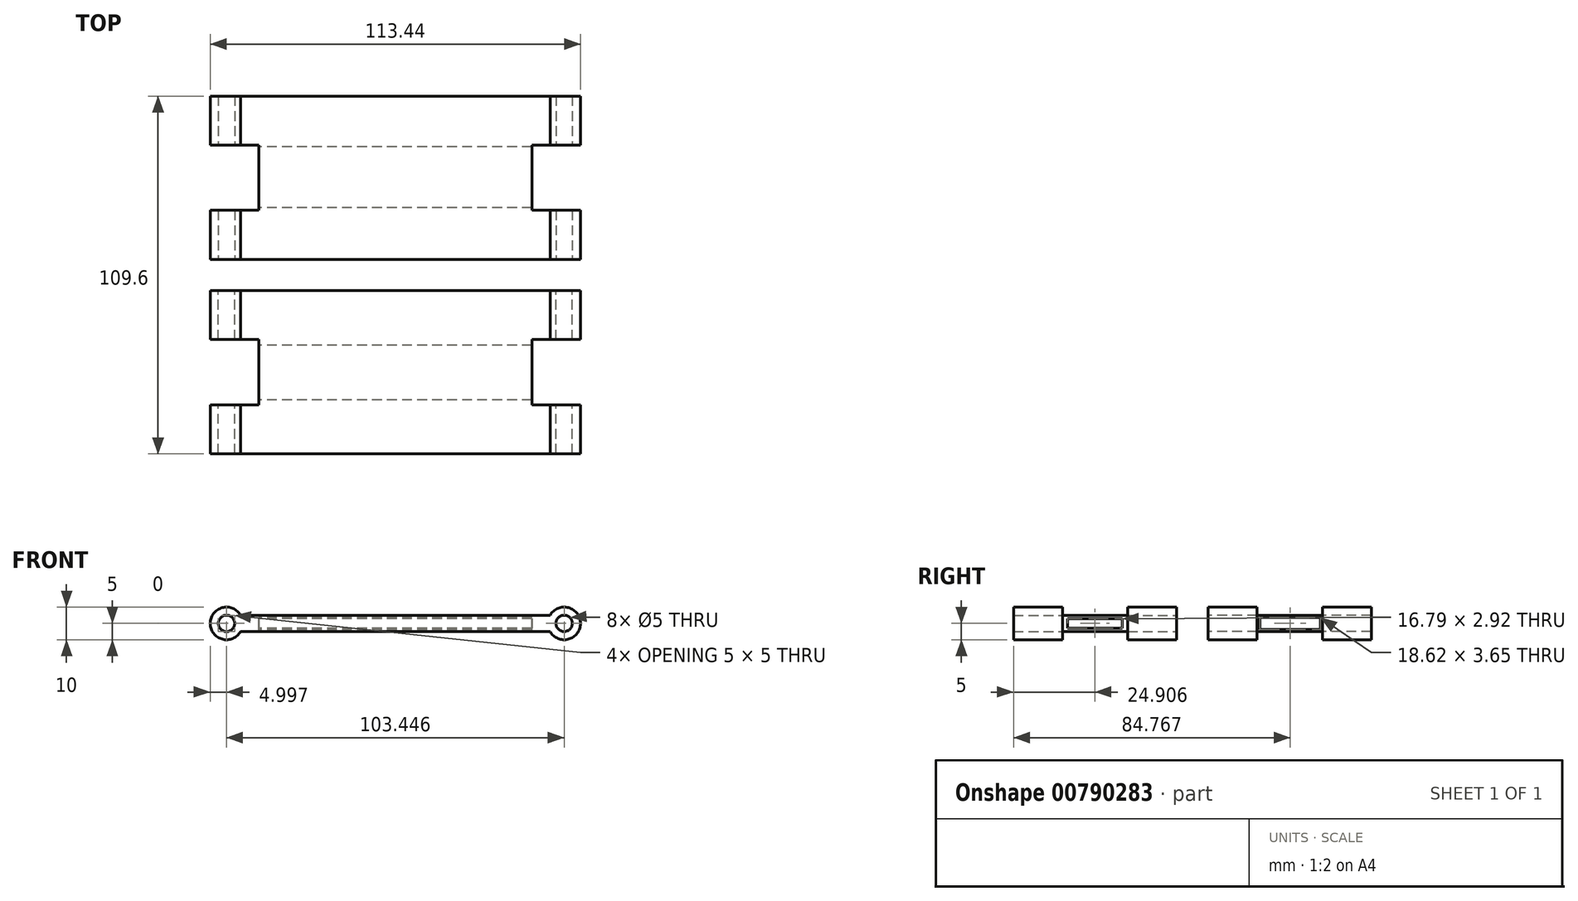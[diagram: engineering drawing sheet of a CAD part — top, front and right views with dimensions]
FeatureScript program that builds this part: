
annotation { "Feature Type Name" : "Feature", "Feature Type Description" : "" }
export const myFeature = defineFeature(function(context is Context, id is Id, definition is map)
    precondition{}
    {
        {
            var Q0;
            Q0=qCreatedBy(makeId("Front.planeOp"),FACE);
            var sketch = newSketch(context, id + "F0", { "sketchPlane" : qUnion([Q0])});
            skLineSegment(sketch, "E0.bottom", {"start": v(55.52, 2.5) * mm, "end": v(-51.72, 2.5) * mm});
            skLineSegment(sketch, "E0.top", {"start": v(55.52, -2.5) * mm, "end": v(-51.72, -2.5) * mm});
            skPoint(sketch, "E0.middle", {"position": v(1.9, 0) * mm});
            skCircle(sketch, "E1", {"center": v(55.52, 0) * mm, "radius": 5 * mm});
            skCircle(sketch, "E2", {"center": v(-51.72, 0) * mm, "radius": 5 * mm});
            skCircle(sketch, "E3", {"center": v(-51.72, 0) * mm, "radius": 2.5 * mm});
            skCircle(sketch, "E4", {"center": v(55.52, 0) * mm, "radius": 2.5 * mm});
            skPoint(sketch, "E5.orphan", {"position": v(-51.72, 2.5) * mm});
            skPoint(sketch, "E6.orphan", {"position": v(-51.72, -2.5) * mm});
            skPoint(sketch, "E7.orphan", {"position": v(55.52, 2.5) * mm});
            skPoint(sketch, "E8.orphan", {"position": v(55.52, -2.5) * mm});
            skSolve(sketch);
        }
        {
            var Q0;
            Q0 = qSketchRegion(id + "F0", true);
            extrude(context, id + "F1", {"entities" : qUnion([Q0]), "depth" : 50 * mm, "offsetDistance" : 25 * mm});
        }
        {
            var Q0;
            Q0=qCreatedBy(makeId("Top.planeOp"),FACE);
            var sketch = newSketch(context, id + "F2", { "sketchPlane" : qUnion([Q0])});
            skLineSegment(sketch, "E9.bottom", {"start": v(-41.88, -35) * mm, "end": v(-70.82, -35) * mm});
            skLineSegment(sketch, "E9.top", {"start": v(-41.88, -15) * mm, "end": v(-70.82, -15) * mm});
            skLineSegment(sketch, "E9.left", {"start": v(-41.88, -35) * mm, "end": v(-41.88, -15) * mm});
            skLineSegment(sketch, "E9.right", {"start": v(-70.82, -35) * mm, "end": v(-70.82, -15) * mm});
            skPoint(sketch, "E9.middle", {"position": v(-56.35, -25) * mm});
            skSolve(sketch);
        }
        {
            var Q0;
            Q0 = qSketchRegion(id + "F2", true);
            extrude(context, id + "F3", {"entities" : qUnion([Q0]), "operationType" : NewBodyOperationType.REMOVE, "oppositeDirection" : true, "depth" : 25 * mm, "offsetDistance" : 25 * mm, "hasSecondDirection" : true, "secondDirectionOppositeDirection" : false, "secondDirectionDepth" : 25 * mm});
        }
        {
            var Q0;
            Q0=qCreatedBy(makeId("Top.planeOp"),FACE);
            var sketch = newSketch(context, id + "F4", { "sketchPlane" : qUnion([Q0])});
            skLineSegment(sketch, "E10.bottom", {"start": v(0, 0) * mm, "end": v(72.18, 0) * mm});
            skLineSegment(sketch, "E10.top", {"start": v(0, -54.93) * mm, "end": v(72.18, -54.93) * mm});
            skLineSegment(sketch, "E10.left", {"start": v(0, 0) * mm, "end": v(0, -54.93) * mm});
            skLineSegment(sketch, "E10.right", {"start": v(72.18, 0) * mm, "end": v(72.18, -54.93) * mm});
            skSolve(sketch);
        }
        {
            var Q0;
            Q0 = qSketchRegion(id + "F4", true);
            extrude(context, id + "F5", {"entities" : qUnion([Q0]), "operationType" : NewBodyOperationType.REMOVE, "oppositeDirection" : true, "depth" : 25 * mm, "offsetDistance" : 25 * mm, "hasSecondDirection" : true, "secondDirectionOppositeDirection" : false, "secondDirectionDepth" : 25 * mm});
        }
        {
            var Q0;
            Q0=makeQuery(id+"F1.opExtrude","SWEPT_BODY",BODY,{"disambiguationData":[OSD([sQuery(id+"F0.wireOp",EDGE,"E0.bottom"),sQuery(id+"F0.wireOp",EDGE,"E0.top"),sQuery(id+"F0.wireOp",EDGE,"E1"),sQuery(id+"F0.wireOp",EDGE,"E2"),sQuery(id+"F0.wireOp",EDGE,"E3"),sQuery(id+"F0.wireOp",EDGE,"E4")])]});
            var Q1;
            Q1=qCreatedBy(makeId("Right.planeOp"),FACE);
            mirror(context, id + "F6", {"operationType" : NewBodyOperationType.ADD, "entities" : qUnion([Q0]), "mirrorPlane" : qUnion([Q1])});
        }
        {
            var Q0;
            Q0=qCreatedBy(makeId("Front.planeOp"),FACE);
            cPlane(context, id + "F7", {"entities" : qUnion([Q0]), "cplaneType" : CPlaneType.OFFSET, "offset" : 4.8 * mm, "oppositeDirection" : true, "width" : 150 * mm, "height" : 150 * mm});
        }
        {
            var Q0;
            Q0=makeQuery(id+"F1.opExtrude","SWEPT_BODY",BODY,{"disambiguationData":[OSD([sQuery(id+"F0.wireOp",EDGE,"E0.bottom"),sQuery(id+"F0.wireOp",EDGE,"E0.top"),sQuery(id+"F0.wireOp",EDGE,"E1"),sQuery(id+"F0.wireOp",EDGE,"E2"),sQuery(id+"F0.wireOp",EDGE,"E3"),sQuery(id+"F0.wireOp",EDGE,"E4")])]});
            var Q1;
            Q1=qCreatedBy(id+"F7.planeOp",FACE);
            mirror(context, id + "F8", {"entities" : qUnion([Q0]), "mirrorPlane" : qUnion([Q1])});
        }
        {
            var Q0;
            Q0=qCreatedBy(makeId("Right.planeOp"),FACE);
            var sketch = newSketch(context, id + "F9", { "sketchPlane" : qUnion([Q0])});
            skLineSegment(sketch, "E11.bottom", {"start": v(-16.7, 1.46) * mm, "end": v(-33.49, 1.46) * mm});
            skLineSegment(sketch, "E11.top", {"start": v(-16.7, -1.46) * mm, "end": v(-33.49, -1.46) * mm});
            skLineSegment(sketch, "E11.left", {"start": v(-16.7, 1.46) * mm, "end": v(-16.7, -1.46) * mm});
            skLineSegment(sketch, "E11.right", {"start": v(-33.49, 1.46) * mm, "end": v(-33.49, -1.46) * mm});
            skPoint(sketch, "E11.middle", {"position": v(-25.1, 0) * mm});
            skSolve(sketch);
        }
        {
            var Q0;
            Q0 = qSketchRegion(id + "F9", true);
            extrude(context, id + "F10", {"entities" : qUnion([Q0]), "operationType" : NewBodyOperationType.REMOVE, "depth" : 63 * mm, "offsetDistance" : 25 * mm, "hasSecondDirection" : true, "secondDirectionOppositeDirection" : true, "secondDirectionDepth" : 65.8 * mm});
        }
        {
            var Q0;
            Q0=qCreatedBy(makeId("Right.planeOp"),FACE);
            var sketch = newSketch(context, id + "F11", { "sketchPlane" : qUnion([Q0])});
            skLineSegment(sketch, "E12.bottom", {"start": v(44.07, -1.83) * mm, "end": v(25.46, -1.83) * mm});
            skLineSegment(sketch, "E12.top", {"start": v(44.07, 1.83) * mm, "end": v(25.46, 1.83) * mm});
            skLineSegment(sketch, "E12.left", {"start": v(44.07, -1.83) * mm, "end": v(44.07, 1.83) * mm});
            skLineSegment(sketch, "E12.right", {"start": v(25.46, -1.83) * mm, "end": v(25.46, 1.83) * mm});
            skPoint(sketch, "E12.middle", {"position": v(34.77, 0) * mm});
            skSolve(sketch);
        }
        {
            var Q0;
            Q0 = qSketchRegion(id + "F11", true);
            extrude(context, id + "F12", {"entities" : qUnion([Q0]), "operationType" : NewBodyOperationType.REMOVE, "depth" : 56.8 * mm, "offsetDistance" : 25 * mm, "hasSecondDirection" : true, "secondDirectionOppositeDirection" : true, "secondDirectionDepth" : 55.3 * mm});
        }
    });
